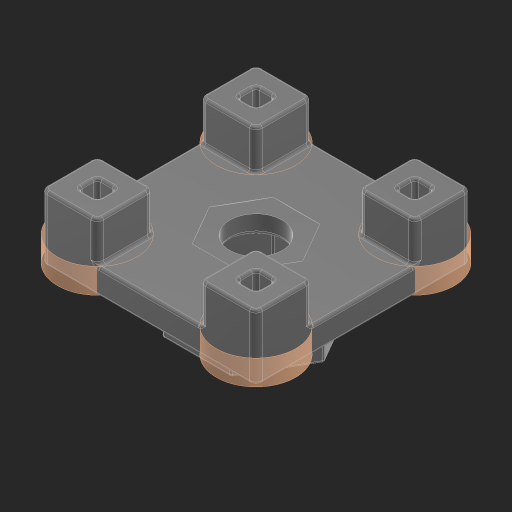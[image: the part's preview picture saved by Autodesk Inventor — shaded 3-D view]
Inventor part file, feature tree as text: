
AUTODESK INVENTOR PART (.ipt)
format: ipt  version: 2023 (Build 270158000, 158)  size: 418,304 bytes
history: native  units: in
note: dims shown in document units (in); Inventor stores cm internally (conversion verified against a paired STEP export)
features: other x4, extrude x4, pattern_linear x1, sketch x1, projected_geometry x1, fillet x1
ambient origin geometry x8: Origin, YZ Plane, XZ Plane, XY Plane, X Axis, Y Axis, Z Axis, Center Point
bodies: Solid1 (feature_tree)
feature tree (12):
  pattern_linear  "Rectangular Pattern1"  Spacing1=0.3937in  [1 undecoded]
  sketch  "Sketch1"  dims[d0=0.25in d1=0.3937in d2=0.0in d3=0.7874in d5=0.5in d6=0.7874in d8=0.5in]
  projected_geometry  "Projected Loop1"
  other  "Srf1"
  other  "Srf2"
  other  "Srf3"
  other  "Srf4"
  fillet  "Fillet10"  Radius=0.7874in
  extrude  "ExtrusionSrf1"  [1 undecoded]
  extrude  "ExtrusionSrf2"  [1 undecoded]
  extrude  "ExtrusionSrf3"  [1 undecoded]
  extrude  "ExtrusionSrf4"  [1 undecoded]
note: 5 required parameter values undecoded (feature->parameter linkage not recoverable at this tier; creation-order binding heuristic only, values carry confidence <= 0.55)
